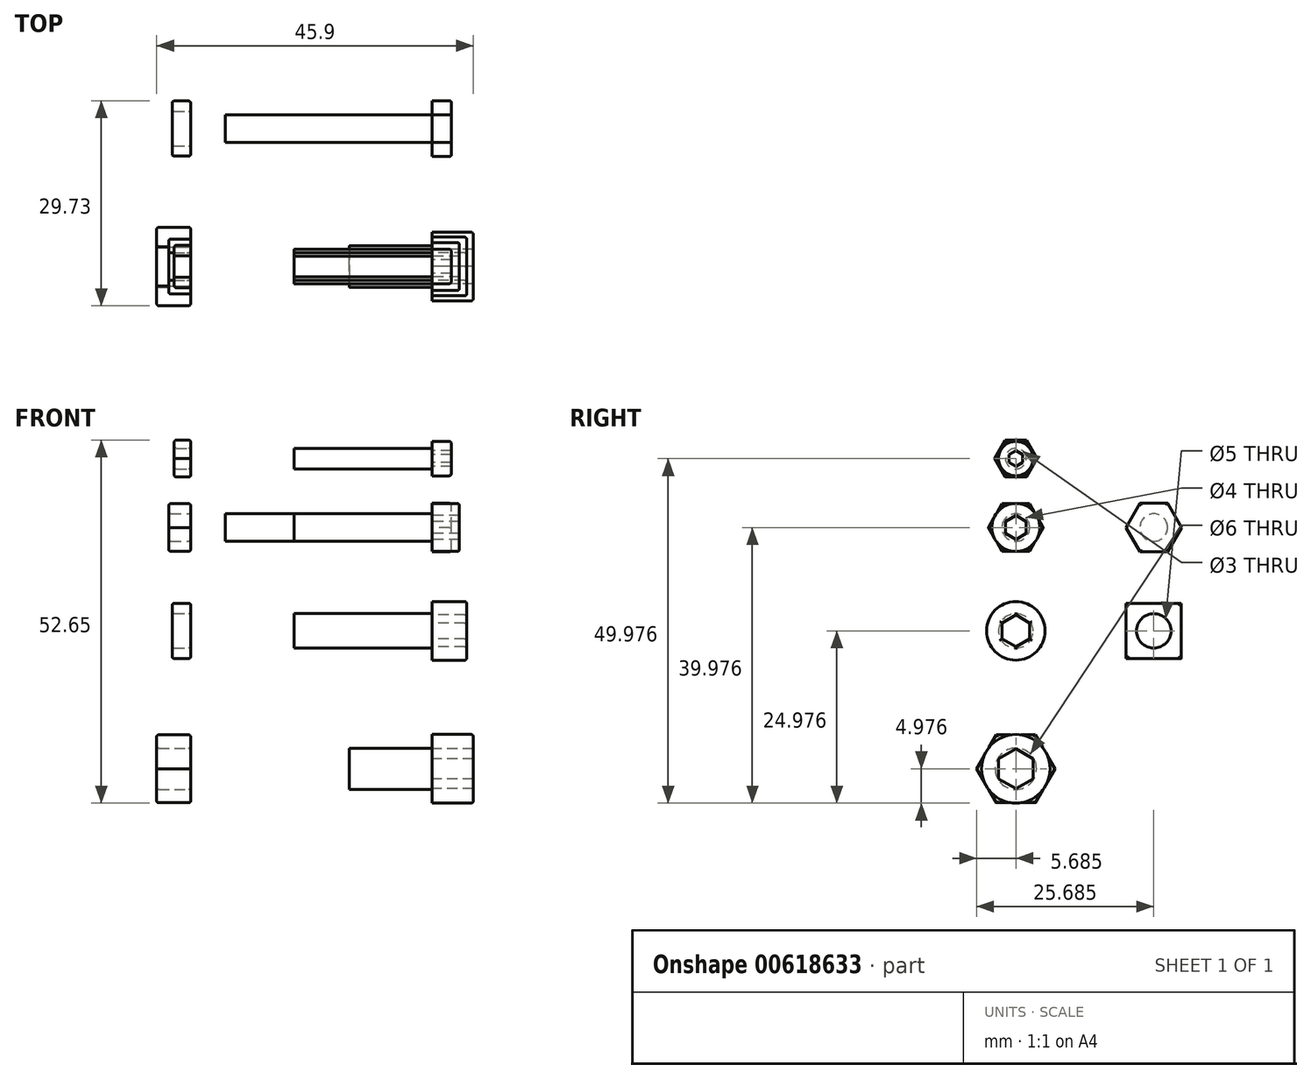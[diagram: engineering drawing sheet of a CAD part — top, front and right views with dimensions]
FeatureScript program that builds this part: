
annotation { "Feature Type Name" : "Feature", "Feature Type Description" : "" }
export const myFeature = defineFeature(function(context is Context, id is Id, definition is map)
    precondition{}
    {
        {
            var Q0;
            Q0=qCreatedBy(makeId("Right.planeOp"),FACE);
            var sketch = newSketch(context, id + "F0", { "sketchPlane" : qUnion([Q0])});
            skCircle(sketch, "E0.cCircle", {"center": v(-28.35, 39.66) * mm, "radius": 2.67 * mm, "construction": true});
            skLineSegment(sketch, "E0.0", {"start": v(-26.81, 36.98) * mm, "end": v(-29.9, 36.98) * mm});
            skLineSegment(sketch, "E0.1", {"start": v(-29.9, 36.98) * mm, "end": v(-31.44, 39.66) * mm});
            skLineSegment(sketch, "E0.2", {"start": v(-31.44, 39.66) * mm, "end": v(-29.9, 42.33) * mm});
            skLineSegment(sketch, "E0.3", {"start": v(-29.9, 42.33) * mm, "end": v(-26.81, 42.33) * mm});
            skLineSegment(sketch, "E0.4", {"start": v(-26.81, 42.33) * mm, "end": v(-25.27, 39.66) * mm});
            skLineSegment(sketch, "E0.5", {"start": v(-25.27, 39.66) * mm, "end": v(-26.81, 36.98) * mm});
            skPoint(sketch, "E0.0.midPoint", {"position": v(-28.35, 36.98) * mm});
            skCircle(sketch, "E1.cCircle", {"center": v(-28.35, 29.66) * mm, "radius": 3.45 * mm, "construction": true});
            skLineSegment(sketch, "E1.0", {"start": v(-26.36, 26.2) * mm, "end": v(-30.35, 26.2) * mm});
            skLineSegment(sketch, "E1.1", {"start": v(-30.35, 26.2) * mm, "end": v(-32.34, 29.66) * mm});
            skLineSegment(sketch, "E1.2", {"start": v(-32.34, 29.66) * mm, "end": v(-30.35, 33.1) * mm});
            skLineSegment(sketch, "E1.3", {"start": v(-30.35, 33.1) * mm, "end": v(-26.36, 33.1) * mm});
            skLineSegment(sketch, "E1.4", {"start": v(-26.36, 33.1) * mm, "end": v(-24.37, 29.66) * mm});
            skLineSegment(sketch, "E1.5", {"start": v(-24.37, 29.66) * mm, "end": v(-26.36, 26.2) * mm});
            skPoint(sketch, "E1.0.midPoint", {"position": v(-28.35, 26.2) * mm});
            skCircle(sketch, "E2.cCircle", {"center": v(-28.35, -5.34) * mm, "radius": 4.92 * mm, "construction": true});
            skLineSegment(sketch, "E2.0", {"start": v(-25.51, -10.27) * mm, "end": v(-31.2, -10.27) * mm});
            skLineSegment(sketch, "E2.1", {"start": v(-31.2, -10.27) * mm, "end": v(-34.04, -5.34) * mm});
            skLineSegment(sketch, "E2.2", {"start": v(-34.04, -5.34) * mm, "end": v(-31.2, -0.42) * mm});
            skLineSegment(sketch, "E2.3", {"start": v(-31.2, -0.42) * mm, "end": v(-25.51, -0.42) * mm});
            skLineSegment(sketch, "E2.4", {"start": v(-25.51, -0.42) * mm, "end": v(-22.67, -5.34) * mm});
            skLineSegment(sketch, "E2.5", {"start": v(-22.67, -5.34) * mm, "end": v(-25.51, -10.27) * mm});
            skPoint(sketch, "E2.0.midPoint", {"position": v(-28.35, -10.27) * mm});
            skCircle(sketch, "E3", {"center": v(-28.35, 39.66) * mm, "radius": 1.5 * mm});
            skCircle(sketch, "E4", {"center": v(-28.35, 29.66) * mm, "radius": 2 * mm});
            skCircle(sketch, "E5", {"center": v(-28.35, -5.34) * mm, "radius": 3 * mm});
            skLineSegment(sketch, "E6.bottom", {"start": v(-4.35, 18.66) * mm, "end": v(-12.35, 18.66) * mm});
            skLineSegment(sketch, "E6.top", {"start": v(-4.35, 10.66) * mm, "end": v(-12.35, 10.66) * mm});
            skLineSegment(sketch, "E6.left", {"start": v(-4.35, 18.66) * mm, "end": v(-4.35, 10.66) * mm});
            skLineSegment(sketch, "E6.right", {"start": v(-12.35, 18.66) * mm, "end": v(-12.35, 10.66) * mm});
            skCircle(sketch, "E7", {"center": v(-8.35, 14.66) * mm, "radius": 2.5 * mm});
            skLineSegment(sketch, "E8", {"start": v(-28.35, 48.47) * mm, "end": v(-28.35, -22.46) * mm, "construction": true});
            skLineSegment(sketch, "E9", {"start": v(-8.35, 48.47) * mm, "end": v(-8.35, -22.46) * mm, "construction": true});
            skPoint(sketch, "E10", {"position": v(-28.35, 14.66) * mm});
            skSolve(sketch);
        }
        {
            var Q0;
            Q0=makeQuery(id+"F0.imprint","IMPRINT",FACE,{"disambiguationData":[TD([[makeQuery(id+"F0.imprint","IMPRINT",EDGE,{"derivedFrom":sQuery(id+"F0.wireOp",EDGE,"E0.0")}),-1.0]])]});
            extrude(context, id + "F1", {"entities" : qUnion([Q0]), "oppositeDirection" : true, "depth" : 2.4 * mm, "offsetDistance" : 25 * mm});
        }
        {
            var Q0;
            Q0=makeQuery(id+"F0.imprint","IMPRINT",FACE,{"disambiguationData":[TD([[makeQuery(id+"F0.imprint","IMPRINT",EDGE,{"derivedFrom":sQuery(id+"F0.wireOp",EDGE,"E1.0")}),-1.0]])]});
            extrude(context, id + "F2", {"entities" : qUnion([Q0]), "oppositeDirection" : true, "depth" : 3.2 * mm, "offsetDistance" : 25 * mm});
        }
        {
            var Q0;
            Q0=makeQuery(id+"F0.imprint","IMPRINT",FACE,{"disambiguationData":[TD([[makeQuery(id+"F0.imprint","IMPRINT",EDGE,{"derivedFrom":sQuery(id+"F0.wireOp",EDGE,"E2.0")}),-1.0]])]});
            extrude(context, id + "F3", {"entities" : qUnion([Q0]), "oppositeDirection" : true, "depth" : 4.95 * mm, "offsetDistance" : 25 * mm});
        }
        {
            var Q0;
            Q0=makeQuery(id+"F0.imprint","IMPRINT",FACE,{"disambiguationData":[TD([[makeQuery(id+"F0.imprint","IMPRINT",EDGE,{"derivedFrom":sQuery(id+"F0.wireOp",EDGE,"E6.bottom")}),1.0]])]});
            extrude(context, id + "F4", {"entities" : qUnion([Q0]), "oppositeDirection" : true, "depth" : 2.7 * mm, "offsetDistance" : 25 * mm});
        }
        {
            var Q0;
            Q0=qCreatedBy(makeId("Right.planeOp"),FACE);
            cPlane(context, id + "F5", {"entities" : qUnion([Q0]), "cplaneType" : CPlaneType.OFFSET, "offset" : 35 * mm, "width" : 150 * mm, "height" : 150 * mm});
        }
        {
            var Q0;
            Q0=qCreatedBy(id+"F5.planeOp",FACE);
            var sketch = newSketch(context, id + "F6", { "sketchPlane" : qUnion([Q0])});
            skPoint(sketch, "E11.0", {"position": v(-28.35, 39.66) * mm});
            skPoint(sketch, "E11.1", {"position": v(-28.35, 29.66) * mm});
            skPoint(sketch, "E11.2", {"position": v(-28.35, -5.34) * mm});
            skCircle(sketch, "E12", {"center": v(-28.35, 39.66) * mm, "radius": 1.5 * mm});
            skCircle(sketch, "E13", {"center": v(-28.35, 29.66) * mm, "radius": 2 * mm});
            skCircle(sketch, "E14", {"center": v(-28.35, -5.34) * mm, "radius": 3 * mm});
            skCircle(sketch, "E15", {"center": v(-28.35, 39.66) * mm, "radius": 2.5 * mm});
            skCircle(sketch, "E16", {"center": v(-28.35, 29.66) * mm, "radius": 3.48 * mm});
            skCircle(sketch, "E17", {"center": v(-28.35, -5.34) * mm, "radius": 4.97 * mm});
            skCircle(sketch, "E18.cCircle", {"center": v(-28.35, -5.34) * mm, "radius": 2.5 * mm, "construction": true});
            skLineSegment(sketch, "E18.0", {"start": v(-25.85, -3.9) * mm, "end": v(-25.85, -6.79) * mm});
            skLineSegment(sketch, "E18.1", {"start": v(-25.85, -6.79) * mm, "end": v(-28.35, -8.23) * mm});
            skLineSegment(sketch, "E18.2", {"start": v(-28.35, -8.23) * mm, "end": v(-30.85, -6.79) * mm});
            skLineSegment(sketch, "E18.3", {"start": v(-30.85, -6.79) * mm, "end": v(-30.85, -3.9) * mm});
            skLineSegment(sketch, "E18.4", {"start": v(-30.85, -3.9) * mm, "end": v(-28.35, -2.46) * mm});
            skLineSegment(sketch, "E18.5", {"start": v(-28.35, -2.46) * mm, "end": v(-25.85, -3.9) * mm});
            skPoint(sketch, "E18.0.midPoint", {"position": v(-25.85, -5.34) * mm});
            skCircle(sketch, "E19.cCircle", {"center": v(-28.35, 29.66) * mm, "radius": 1.5 * mm, "construction": true});
            skLineSegment(sketch, "E19.0", {"start": v(-26.85, 30.52) * mm, "end": v(-26.85, 28.79) * mm});
            skLineSegment(sketch, "E19.1", {"start": v(-26.85, 28.79) * mm, "end": v(-28.35, 27.92) * mm});
            skLineSegment(sketch, "E19.2", {"start": v(-28.35, 27.92) * mm, "end": v(-29.85, 28.79) * mm});
            skLineSegment(sketch, "E19.3", {"start": v(-29.85, 28.79) * mm, "end": v(-29.85, 30.52) * mm});
            skLineSegment(sketch, "E19.4", {"start": v(-29.85, 30.52) * mm, "end": v(-28.35, 31.39) * mm});
            skLineSegment(sketch, "E19.5", {"start": v(-28.35, 31.39) * mm, "end": v(-26.85, 30.52) * mm});
            skPoint(sketch, "E19.0.midPoint", {"position": v(-26.85, 29.66) * mm});
            skCircle(sketch, "E20.cCircle", {"center": v(-28.35, 39.66) * mm, "radius": 1 * mm, "construction": true});
            skLineSegment(sketch, "E20.0", {"start": v(-27.35, 40.23) * mm, "end": v(-27.35, 39.08) * mm});
            skLineSegment(sketch, "E20.1", {"start": v(-27.35, 39.08) * mm, "end": v(-28.35, 38.5) * mm});
            skLineSegment(sketch, "E20.2", {"start": v(-28.35, 38.5) * mm, "end": v(-29.35, 39.08) * mm});
            skLineSegment(sketch, "E20.3", {"start": v(-29.35, 39.08) * mm, "end": v(-29.35, 40.23) * mm});
            skLineSegment(sketch, "E20.4", {"start": v(-29.35, 40.23) * mm, "end": v(-28.35, 40.81) * mm});
            skLineSegment(sketch, "E20.5", {"start": v(-28.35, 40.81) * mm, "end": v(-27.35, 40.23) * mm});
            skPoint(sketch, "E20.0.midPoint", {"position": v(-27.35, 39.66) * mm});
            skPoint(sketch, "E21", {"position": v(-8.35, 29.66) * mm});
            skCircle(sketch, "E22", {"center": v(-8.35, 29.66) * mm, "radius": 2 * mm});
            skCircle(sketch, "E23.cCircle", {"center": v(-8.35, 29.66) * mm, "radius": 3.5 * mm, "construction": true});
            skLineSegment(sketch, "E23.0", {"start": v(-10.38, 33.16) * mm, "end": v(-6.33, 33.16) * mm});
            skLineSegment(sketch, "E23.1", {"start": v(-6.33, 33.16) * mm, "end": v(-4.31, 29.66) * mm});
            skLineSegment(sketch, "E23.2", {"start": v(-4.31, 29.66) * mm, "end": v(-6.33, 26.16) * mm});
            skLineSegment(sketch, "E23.3", {"start": v(-6.33, 26.16) * mm, "end": v(-10.38, 26.16) * mm});
            skLineSegment(sketch, "E23.4", {"start": v(-10.38, 26.16) * mm, "end": v(-12.4, 29.66) * mm});
            skLineSegment(sketch, "E23.5", {"start": v(-12.4, 29.66) * mm, "end": v(-10.38, 33.16) * mm});
            skPoint(sketch, "E23.0.midPoint", {"position": v(-8.35, 33.16) * mm});
            skPoint(sketch, "E24.0", {"position": v(-8.35, 14.66) * mm});
            skPoint(sketch, "E25.0", {"position": v(-28.35, 14.66) * mm});
            skCircle(sketch, "E26", {"center": v(-28.35, 14.66) * mm, "radius": 2.5 * mm});
            skCircle(sketch, "E27", {"center": v(-28.35, 14.66) * mm, "radius": 4.25 * mm});
            skCircle(sketch, "E28.cCircle", {"center": v(-28.35, 14.66) * mm, "radius": 2 * mm, "construction": true});
            skLineSegment(sketch, "E28.0", {"start": v(-26.35, 15.81) * mm, "end": v(-26.35, 13.5) * mm});
            skLineSegment(sketch, "E28.1", {"start": v(-26.35, 13.5) * mm, "end": v(-28.35, 12.35) * mm});
            skLineSegment(sketch, "E28.2", {"start": v(-28.35, 12.35) * mm, "end": v(-30.35, 13.5) * mm});
            skLineSegment(sketch, "E28.3", {"start": v(-30.35, 13.5) * mm, "end": v(-30.35, 15.81) * mm});
            skLineSegment(sketch, "E28.4", {"start": v(-30.35, 15.81) * mm, "end": v(-28.35, 16.96) * mm});
            skLineSegment(sketch, "E28.5", {"start": v(-28.35, 16.96) * mm, "end": v(-26.35, 15.81) * mm});
            skPoint(sketch, "E28.0.midPoint", {"position": v(-26.35, 14.66) * mm});
            skSolve(sketch);
        }
        {
            var Q0;
            Q0=makeQuery(id+"F6.imprint","IMPRINT",FACE,{"disambiguationData":[TD([[makeQuery(id+"F6.imprint","IMPRINT",EDGE,{"derivedFrom":sQuery(id+"F6.wireOp",EDGE,"E12")}),1.0]])]});
            var Q1;
            Q1=makeQuery(id+"F6.imprint","IMPRINT",FACE,{"disambiguationData":[TD([[makeQuery(id+"F6.imprint","IMPRINT",EDGE,{"derivedFrom":sQuery(id+"F6.wireOp",EDGE,"E20.0")}),-1.0]])]});
            extrude(context, id + "F7", {"entities" : qUnion([Q0, Q1]), "oppositeDirection" : true, "depth" : 20 * mm, "offsetDistance" : 25 * mm});
        }
        {
            var Q0;
            Q0=makeQuery(id+"F6.imprint","IMPRINT",FACE,{"disambiguationData":[TD([[makeQuery(id+"F6.imprint","IMPRINT",EDGE,{"derivedFrom":sQuery(id+"F6.wireOp",EDGE,"E13")}),1.0]])]});
            var Q1;
            Q1=makeQuery(id+"F6.imprint","IMPRINT",FACE,{"disambiguationData":[TD([[makeQuery(id+"F6.imprint","IMPRINT",EDGE,{"derivedFrom":sQuery(id+"F6.wireOp",EDGE,"E19.0")}),-1.0]])]});
            extrude(context, id + "F8", {"entities" : qUnion([Q0, Q1]), "oppositeDirection" : true, "depth" : 20 * mm, "offsetDistance" : 25 * mm});
        }
        {
            var Q0;
            Q0=makeQuery(id+"F6.imprint","IMPRINT",FACE,{"disambiguationData":[TD([[makeQuery(id+"F6.imprint","IMPRINT",EDGE,{"derivedFrom":sQuery(id+"F6.wireOp",EDGE,"E18.0")}),-1.0]])]});
            var Q1;
            Q1=makeQuery(id+"F6.imprint","IMPRINT",FACE,{"disambiguationData":[TD([[makeQuery(id+"F6.imprint","IMPRINT",EDGE,{"derivedFrom":sQuery(id+"F6.wireOp",EDGE,"E14")}),1.0]])]});
            extrude(context, id + "F9", {"entities" : qUnion([Q0, Q1]), "oppositeDirection" : true, "depth" : 12 * mm, "offsetDistance" : 25 * mm});
        }
        {
            var Q0;
            Q0=makeQuery(id+"F6.imprint","IMPRINT",FACE,{"disambiguationData":[TD([[makeQuery(id+"F6.imprint","IMPRINT",EDGE,{"derivedFrom":sQuery(id+"F6.wireOp",EDGE,"E12")}),-1.0]])]});
            var Q1;
            Q1=makeQuery(id+"F6.imprint","IMPRINT",FACE,{"disambiguationData":[TD([[makeQuery(id+"F6.imprint","IMPRINT",EDGE,{"derivedFrom":sQuery(id+"F6.wireOp",EDGE,"E12")}),1.0]])]});
            extrude(context, id + "F10", {"entities" : qUnion([Q0, Q1]), "operationType" : NewBodyOperationType.ADD, "depth" : 2.75 * mm, "offsetDistance" : 25 * mm});
        }
        {
            var Q0;
            Q0=makeQuery(id+"F6.imprint","IMPRINT",FACE,{"disambiguationData":[TD([[makeQuery(id+"F6.imprint","IMPRINT",EDGE,{"derivedFrom":sQuery(id+"F6.wireOp",EDGE,"E13")}),1.0]])]});
            var Q1;
            Q1=makeQuery(id+"F6.imprint","IMPRINT",FACE,{"disambiguationData":[TD([[makeQuery(id+"F6.imprint","IMPRINT",EDGE,{"derivedFrom":sQuery(id+"F6.wireOp",EDGE,"E13")}),-1.0]])]});
            extrude(context, id + "F11", {"entities" : qUnion([Q0, Q1]), "operationType" : NewBodyOperationType.ADD, "depth" : 3.95 * mm, "offsetDistance" : 25 * mm});
        }
        {
            var Q0;
            Q0=makeQuery(id+"F6.imprint","IMPRINT",FACE,{"disambiguationData":[TD([[makeQuery(id+"F6.imprint","IMPRINT",EDGE,{"derivedFrom":sQuery(id+"F6.wireOp",EDGE,"E14")}),1.0]])]});
            var Q1;
            Q1=makeQuery(id+"F6.imprint","IMPRINT",FACE,{"disambiguationData":[TD([[makeQuery(id+"F6.imprint","IMPRINT",EDGE,{"derivedFrom":sQuery(id+"F6.wireOp",EDGE,"E14")}),-1.0]])]});
            extrude(context, id + "F12", {"entities" : qUnion([Q0, Q1]), "operationType" : NewBodyOperationType.ADD, "depth" : 5.95 * mm, "offsetDistance" : 25 * mm});
        }
        {
            var Q0;
            Q0=makeQuery(id+"F6.imprint","IMPRINT",FACE,{"disambiguationData":[TD([[makeQuery(id+"F6.imprint","IMPRINT",EDGE,{"derivedFrom":sQuery(id+"F6.wireOp",EDGE,"E22")}),1.0]])]});
            var Q1;
            Q1=makeQuery(id+"F6.imprint","IMPRINT",FACE,{"disambiguationData":[TD([[makeQuery(id+"F6.imprint","IMPRINT",EDGE,{"derivedFrom":sQuery(id+"F6.wireOp",EDGE,"E22")}),-1.0]])]});
            extrude(context, id + "F13", {"entities" : qUnion([Q0, Q1]), "depth" : 2.8 * mm, "offsetDistance" : 25 * mm});
        }
        {
            var Q0;
            Q0=makeQuery(id+"F6.imprint","IMPRINT",FACE,{"disambiguationData":[TD([[makeQuery(id+"F6.imprint","IMPRINT",EDGE,{"derivedFrom":sQuery(id+"F6.wireOp",EDGE,"E22")}),1.0]])]});
            extrude(context, id + "F14", {"entities" : qUnion([Q0]), "operationType" : NewBodyOperationType.ADD, "oppositeDirection" : true, "depth" : 30 * mm, "offsetDistance" : 25 * mm});
        }
        {
            var Q0;
            Q0=makeQuery(id+"F6.imprint","IMPRINT",FACE,{"disambiguationData":[TD([[makeQuery(id+"F6.imprint","IMPRINT",EDGE,{"derivedFrom":sQuery(id+"F6.wireOp",EDGE,"E26")}),-1.0]])]});
            var Q1;
            Q1=makeQuery(id+"F6.imprint","IMPRINT",FACE,{"disambiguationData":[TD([[makeQuery(id+"F6.imprint","IMPRINT",EDGE,{"derivedFrom":sQuery(id+"F6.wireOp",EDGE,"E26")}),1.0]])]});
            extrude(context, id + "F15", {"entities" : qUnion([Q0, Q1]), "depth" : 5 * mm, "offsetDistance" : 25 * mm});
        }
        {
            var Q0;
            Q0=makeQuery(id+"F6.imprint","IMPRINT",FACE,{"disambiguationData":[TD([[makeQuery(id+"F6.imprint","IMPRINT",EDGE,{"derivedFrom":sQuery(id+"F6.wireOp",EDGE,"E26")}),1.0]])]});
            var Q1;
            Q1=makeQuery(id+"F6.imprint","IMPRINT",FACE,{"disambiguationData":[TD([[makeQuery(id+"F6.imprint","IMPRINT",EDGE,{"derivedFrom":sQuery(id+"F6.wireOp",EDGE,"E28.0")}),-1.0]])]});
            extrude(context, id + "F16", {"entities" : qUnion([Q0, Q1]), "operationType" : NewBodyOperationType.ADD, "oppositeDirection" : true, "depth" : 20 * mm, "offsetDistance" : 25 * mm});
        }
        {
            var Q0;
            Q0=makeQuery(id+"F12.opExtrude","CAP_EDGE",EDGE,{"disambiguationData":[OSD([sQuery(id+"F6.wireOp",EDGE,"E17")])],"isStart":false});
            var Q1;
            Q1=makeQuery(id+"F13.opExtrude","CAP_FACE",FACE,{"disambiguationData":[OSD([sQuery(id+"F6.wireOp",EDGE,"E23.0"),sQuery(id+"F6.wireOp",EDGE,"E23.1"),sQuery(id+"F6.wireOp",EDGE,"E23.2"),sQuery(id+"F6.wireOp",EDGE,"E23.3"),sQuery(id+"F6.wireOp",EDGE,"E23.4"),sQuery(id+"F6.wireOp",EDGE,"E23.5")])],"isStart":false});
            var Q2;
            Q2=makeQuery(id+"F11.opExtrude","CAP_EDGE",EDGE,{"disambiguationData":[OSD([sQuery(id+"F6.wireOp",EDGE,"E16")])],"isStart":false});
            var Q3;
            Q3=makeQuery(id+"F10.opExtrude","CAP_EDGE",EDGE,{"disambiguationData":[OSD([sQuery(id+"F6.wireOp",EDGE,"E15")])],"isStart":false});
            var Q4;
            Q4=makeQuery(id+"F1.opExtrude","CAP_FACE",FACE,{"disambiguationData":[OSD([sQuery(id+"F0.wireOp",EDGE,"E0.0"),sQuery(id+"F0.wireOp",EDGE,"E0.1"),sQuery(id+"F0.wireOp",EDGE,"E0.2"),sQuery(id+"F0.wireOp",EDGE,"E0.3"),sQuery(id+"F0.wireOp",EDGE,"E0.4"),sQuery(id+"F0.wireOp",EDGE,"E0.5"),sQuery(id+"F0.wireOp",EDGE,"E3")])],"isStart":true});
            var Q5;
            Q5=makeQuery(id+"F1.opExtrude","CAP_FACE",FACE,{"disambiguationData":[OSD([sQuery(id+"F0.wireOp",EDGE,"E0.0"),sQuery(id+"F0.wireOp",EDGE,"E0.1"),sQuery(id+"F0.wireOp",EDGE,"E0.2"),sQuery(id+"F0.wireOp",EDGE,"E0.3"),sQuery(id+"F0.wireOp",EDGE,"E0.4"),sQuery(id+"F0.wireOp",EDGE,"E0.5"),sQuery(id+"F0.wireOp",EDGE,"E3")])],"isStart":false});
            var Q6;
            Q6=makeQuery(id+"F2.opExtrude","CAP_FACE",FACE,{"disambiguationData":[OSD([sQuery(id+"F0.wireOp",EDGE,"E1.0"),sQuery(id+"F0.wireOp",EDGE,"E1.1"),sQuery(id+"F0.wireOp",EDGE,"E1.2"),sQuery(id+"F0.wireOp",EDGE,"E1.3"),sQuery(id+"F0.wireOp",EDGE,"E1.4"),sQuery(id+"F0.wireOp",EDGE,"E1.5"),sQuery(id+"F0.wireOp",EDGE,"E4")])],"isStart":false});
            var Q7;
            Q7=makeQuery(id+"F3.opExtrude","CAP_FACE",FACE,{"disambiguationData":[OSD([sQuery(id+"F0.wireOp",EDGE,"E2.0"),sQuery(id+"F0.wireOp",EDGE,"E2.1"),sQuery(id+"F0.wireOp",EDGE,"E2.2"),sQuery(id+"F0.wireOp",EDGE,"E2.3"),sQuery(id+"F0.wireOp",EDGE,"E2.4"),sQuery(id+"F0.wireOp",EDGE,"E2.5"),sQuery(id+"F0.wireOp",EDGE,"E5")])],"isStart":false});
            var Q8;
            Q8=makeQuery(id+"F2.opExtrude","CAP_FACE",FACE,{"disambiguationData":[OSD([sQuery(id+"F0.wireOp",EDGE,"E1.0"),sQuery(id+"F0.wireOp",EDGE,"E1.1"),sQuery(id+"F0.wireOp",EDGE,"E1.2"),sQuery(id+"F0.wireOp",EDGE,"E1.3"),sQuery(id+"F0.wireOp",EDGE,"E1.4"),sQuery(id+"F0.wireOp",EDGE,"E1.5"),sQuery(id+"F0.wireOp",EDGE,"E4")])],"isStart":true});
            var Q9;
            Q9=makeQuery(id+"F3.opExtrude","CAP_FACE",FACE,{"disambiguationData":[OSD([sQuery(id+"F0.wireOp",EDGE,"E2.0"),sQuery(id+"F0.wireOp",EDGE,"E2.1"),sQuery(id+"F0.wireOp",EDGE,"E2.2"),sQuery(id+"F0.wireOp",EDGE,"E2.3"),sQuery(id+"F0.wireOp",EDGE,"E2.4"),sQuery(id+"F0.wireOp",EDGE,"E2.5"),sQuery(id+"F0.wireOp",EDGE,"E5")])],"isStart":true});
            var Q10;
            Q10=makeQuery(id+"F4.opExtrude","CAP_FACE",FACE,{"disambiguationData":[OSD([sQuery(id+"F0.wireOp",EDGE,"E6.bottom"),sQuery(id+"F0.wireOp",EDGE,"E6.top"),sQuery(id+"F0.wireOp",EDGE,"E6.left"),sQuery(id+"F0.wireOp",EDGE,"E6.right"),sQuery(id+"F0.wireOp",EDGE,"E7")])],"isStart":true});
            var Q11;
            Q11=makeQuery(id+"F4.opExtrude","CAP_FACE",FACE,{"disambiguationData":[OSD([sQuery(id+"F0.wireOp",EDGE,"E6.bottom"),sQuery(id+"F0.wireOp",EDGE,"E6.top"),sQuery(id+"F0.wireOp",EDGE,"E6.left"),sQuery(id+"F0.wireOp",EDGE,"E6.right"),sQuery(id+"F0.wireOp",EDGE,"E7")])],"isStart":false});
            var Q12;
            Q12=makeQuery(id+"F15.opExtrude","CAP_FACE",FACE,{"disambiguationData":[OSD([sQuery(id+"F6.wireOp",EDGE,"E27"),sQuery(id+"F6.wireOp",EDGE,"E28.0"),sQuery(id+"F6.wireOp",EDGE,"E28.1"),sQuery(id+"F6.wireOp",EDGE,"E28.2"),sQuery(id+"F6.wireOp",EDGE,"E28.3"),sQuery(id+"F6.wireOp",EDGE,"E28.4"),sQuery(id+"F6.wireOp",EDGE,"E28.5")])],"isStart":false});
            fillet(context, id + "F17", {"entities" : qUnion([Q0, Q1, Q2, Q3, Q4, Q5, Q6, Q7, Q8, Q9, Q10, Q11, Q12]), "radius" : 0.3 * mm, "tangentPropagation" : true, "allowEdgeOverflow" : false});
        }
    });
